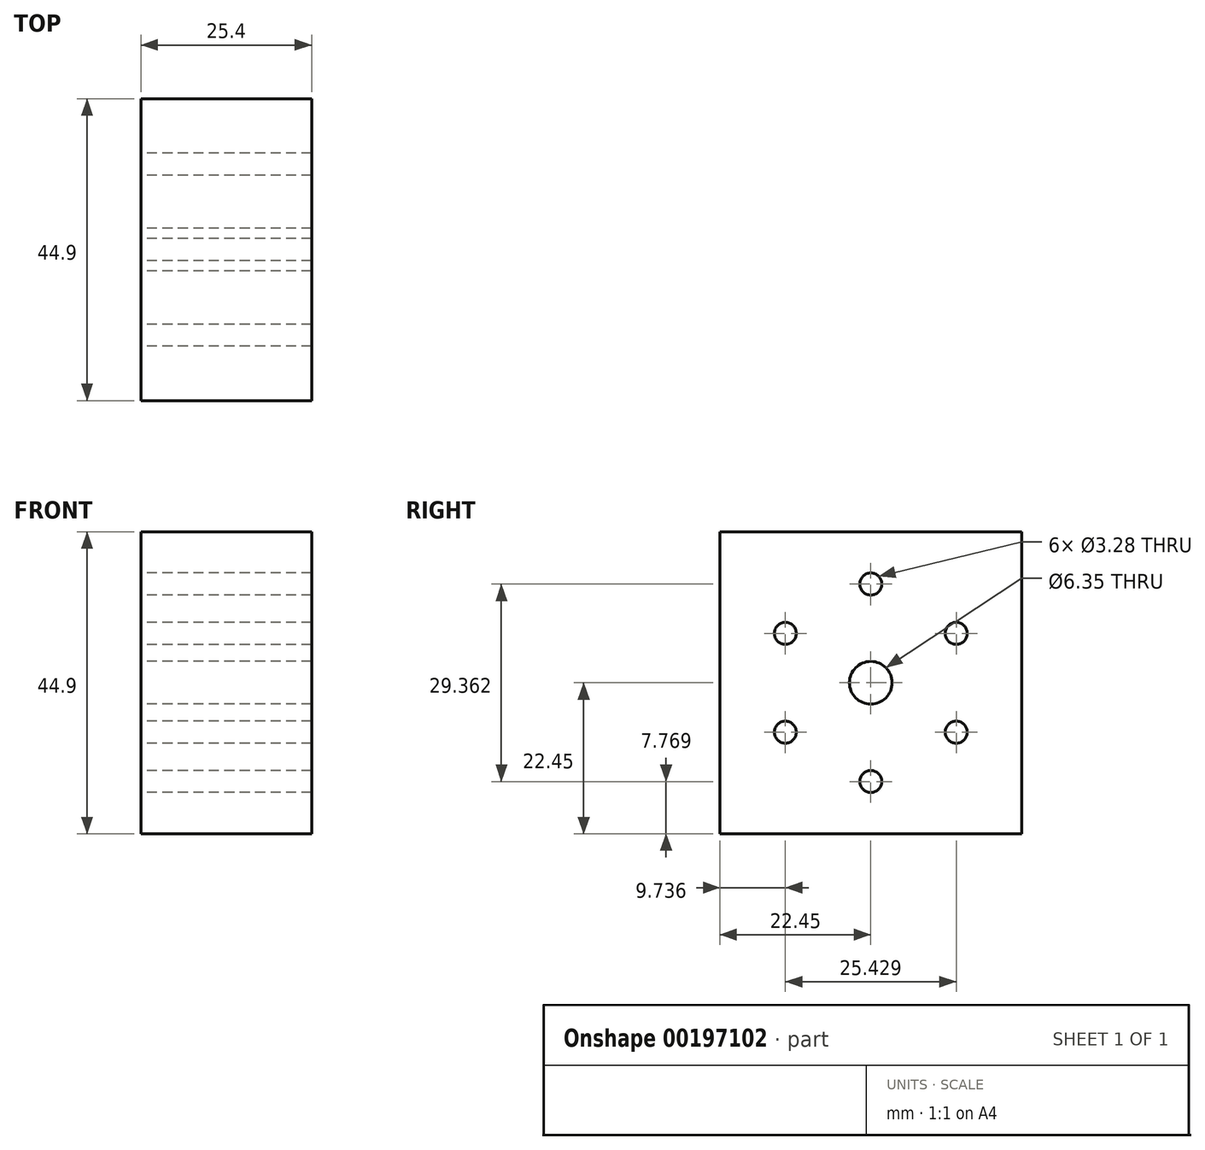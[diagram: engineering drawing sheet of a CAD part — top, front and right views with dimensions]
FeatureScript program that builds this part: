
annotation { "Feature Type Name" : "Feature", "Feature Type Description" : "" }
export const myFeature = defineFeature(function(context is Context, id is Id, definition is map)
    precondition{}
    {
        {
            var Q0;
            Q0=qCreatedBy(makeId("Right.planeOp"),FACE);
            var sketch = newSketch(context, id + "F0", { "sketchPlane" : qUnion([Q0])});
            skLineSegment(sketch, "E0.bottom", {"start": v(-22.45, 22.45) * mm, "end": v(22.45, 22.45) * mm});
            skLineSegment(sketch, "E0.top", {"start": v(-22.45, -22.45) * mm, "end": v(22.45, -22.45) * mm});
            skLineSegment(sketch, "E0.left", {"start": v(-22.45, 22.45) * mm, "end": v(-22.45, -22.45) * mm});
            skLineSegment(sketch, "E0.right", {"start": v(22.45, 22.45) * mm, "end": v(22.45, -22.45) * mm});
            skLineSegment(sketch, "E1", {"start": v(-22.45, 0) * mm, "end": v(-3.18, 0) * mm, "construction": true});
            skCircle(sketch, "E2", {"center": v(0, 0) * mm, "radius": 3.18 * mm});
            skLineSegment(sketch, "E3.trimOffspring", {"start": v(3.17, 0) * mm, "end": v(22.45, 0) * mm, "construction": true});
            skLineSegment(sketch, "E4", {"start": v(0, 22.45) * mm, "end": v(0, 3.18) * mm, "construction": true});
            skLineSegment(sketch, "E5.trimOffspring", {"start": v(0, -3.18) * mm, "end": v(0, -22.45) * mm, "construction": true});
            skCircle(sketch, "E6", {"center": v(0, 14.68) * mm, "radius": 1.64 * mm});
            skCircle(sketch, "E7.1.0", {"center": v(-12.71, 7.34) * mm, "radius": 1.64 * mm});
            skCircle(sketch, "E7.2.0", {"center": v(-12.71, -7.34) * mm, "radius": 1.64 * mm});
            skCircle(sketch, "E7.3.0", {"center": v(0, -14.68) * mm, "radius": 1.64 * mm});
            skCircle(sketch, "E7.4.0", {"center": v(12.71, -7.34) * mm, "radius": 1.64 * mm});
            skCircle(sketch, "E7.5.0", {"center": v(12.71, 7.34) * mm, "radius": 1.64 * mm});
            skSolve(sketch);
        }
        {
            var Q0;
            Q0=makeQuery(id+"F0.imprint","IMPRINT",FACE,{"disambiguationData":[TD([[makeQuery(id+"F0.imprint","IMPRINT",EDGE,{"derivedFrom":sQuery(id+"F0.wireOp",EDGE,"E0.bottom")}),-1.0]])]});
            extrude(context, id + "F1", {"entities" : qUnion([Q0]), "endBound" : BoundingType.SYMMETRIC, "depth" : 25.4 * mm, "offsetDistance" : 25.4 * mm});
        }
    });
